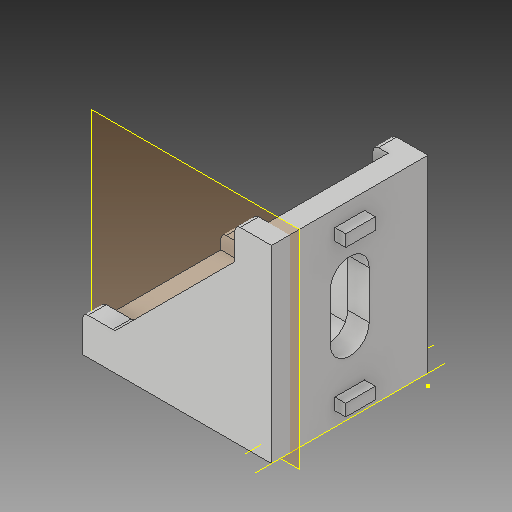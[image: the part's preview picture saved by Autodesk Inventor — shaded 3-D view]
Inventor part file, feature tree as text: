
AUTODESK INVENTOR PART (.ipt)
format: ipt  version: 2018 (Build 220112000, 112)  size: 186,880 bytes
history: native  units: mm
features: sketch x8, other x5, plane x1
ambient origin geometry x8: Origin, YZ Plane, XZ Plane, XY Plane, X Axis, Y Axis, Z Axis, Center Point
bodies: Solid1 (feature_tree)
feature tree (14):
  other  "30mm Bracket_CPY_MIR2.ipt"
  other  "Solid1::30mm Bracket_CPY_MIR2.ipt"
  other  "TaggingFeature1"
  sketch  "Sketch1"  dims[d0=10.0mm]
  sketch  "Sketch2"
  sketch  "Sketch3"
  sketch  "Sketch4"
  sketch  "Sketch5"
  sketch  "Sketch7"
  sketch  "Sketch9"
  sketch  "Sketch10"
  plane  "Work Plane1"
  other  "Work Axis1"
  other  "Work Axis2"
